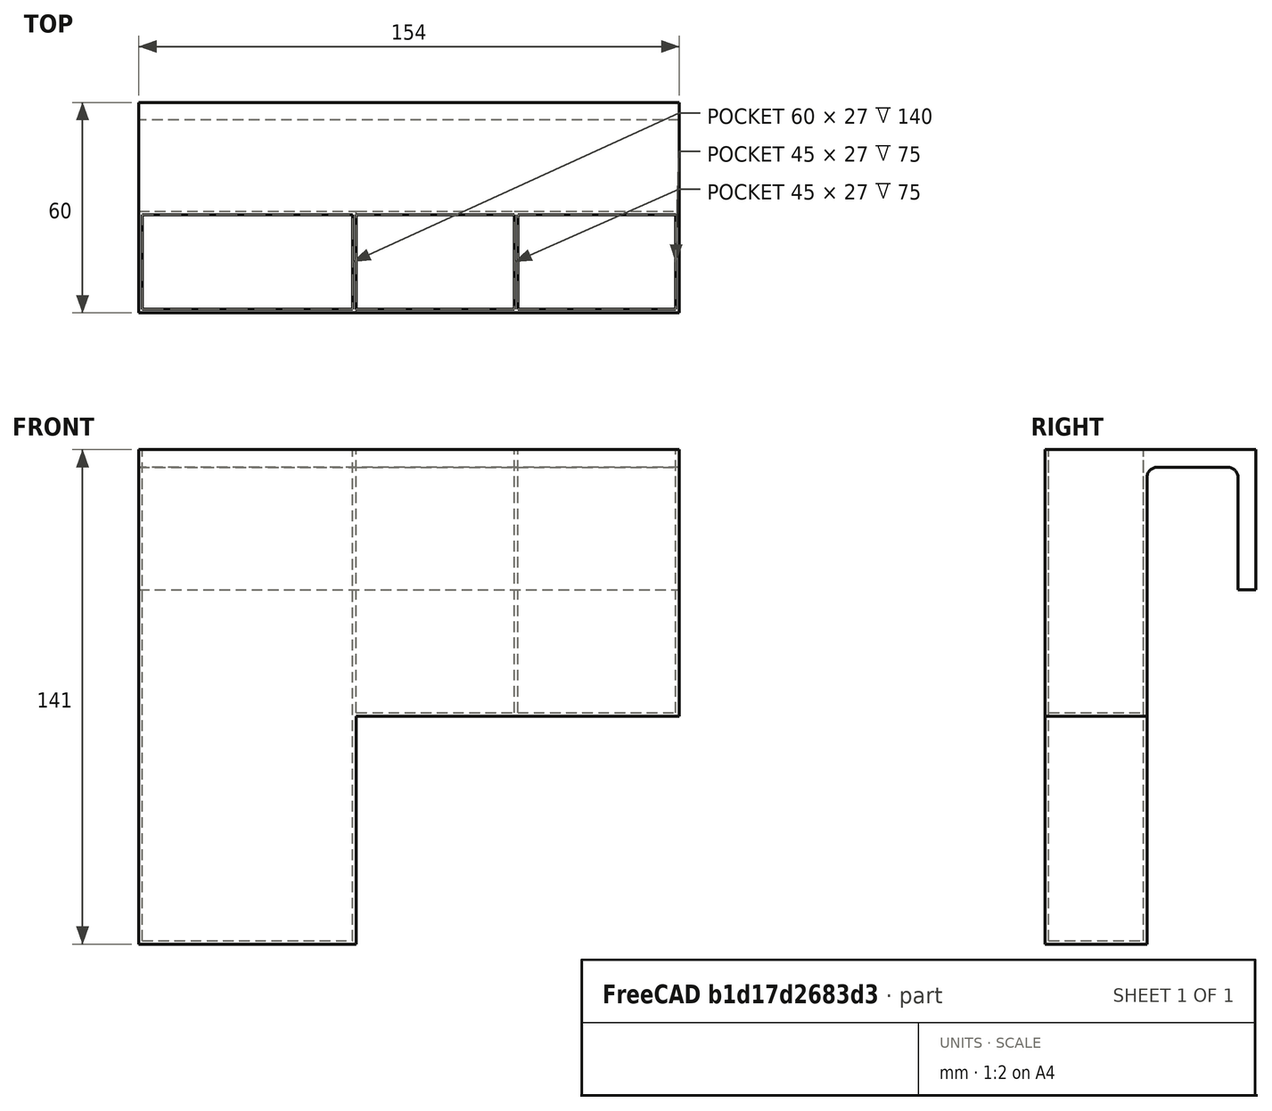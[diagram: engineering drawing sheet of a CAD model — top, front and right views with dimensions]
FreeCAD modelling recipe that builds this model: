
FCSTD DOCUMENT  (FreeCAD 1.0R1.0.1)
Label: TV Remote Holder
License: All rights reserved
LicenseURL: http://en.wikipedia.org/wiki/All_rights_reserved
objects: Part::Box×8, Part::MultiFuse×3, Part::Cut×1, Part::Fillet×1
note: 13 computed .brp shape members not serialized (recipe doc carries the construction recipe); baked Part::Feature solids carry a one-line shape summary decoded from their .brp

FEATURE [Part::Box] Box  label="Cube"
  AttacherType = Attacher::AttachEngine3D
  Height = 141
  Length = 62
  Width = 29
FEATURE [Part::Box] Box001  label="Cube001"
  AttacherType = Attacher::AttachEngine3D
  Height = 140
  Length = 60
  Placement = pos=(1,1,1) rot=(0,0,1;0rad)
  Width = 27
FEATURE [Part::Box] Box002  label="Cube002"
  AttacherType = Attacher::AttachEngine3D
  Height = 76
  Length = 47
  Placement = pos=(61,0,65) rot=(0,0,1;0rad)
  Width = 29
FEATURE [Part::Box] Box003  label="Cube003"
  AttacherType = Attacher::AttachEngine3D
  Height = 75
  Length = 45
  Placement = pos=(62,1,66) rot=(0,0,1;0rad)
  Width = 27
FEATURE [Part::Box] Box004  label="Cube004"
  AttacherType = Attacher::AttachEngine3D
  Height = 76
  Length = 47
  Placement = pos=(107,0,65) rot=(0,0,1;0rad)
  Width = 29
FEATURE [Part::Box] Box005  label="Cube005"
  AttacherType = Attacher::AttachEngine3D
  Height = 75
  Length = 45
  Placement = pos=(108,1,66) rot=(0,0,1;0rad)
  Width = 27
FEATURE [Part::MultiFuse] Fusion
  Shapes = -> [Box,Box002,Box004]
FEATURE [Part::MultiFuse] Fusion001
  Shapes = -> [Box001,Box003,Box005]
FEATURE [Part::Box] Box006  label="Cube006"
  AttacherType = Attacher::AttachEngine3D
  Height = 5
  Length = 154
  Placement = pos=(0,29,136) rot=(0,0,1;0rad)
  Width = 31
FEATURE [Part::Box] Box007  label="Cube007"
  AttacherType = Attacher::AttachEngine3D
  Height = 40
  Length = 154
  Placement = pos=(0,55,101) rot=(0,0,1;0rad)
  Width = 5
FEATURE [Part::MultiFuse] Fusion002
  Shapes = -> [Fusion,Box006,Box007]
FEATURE [Part::Cut] Cut
  Base = -> Fusion002
  Tool = -> Fusion001
FEATURE [Part::Fillet] Fillet
  Base = -> Cut
  EdgeLinks = -> Cut [Edge19,Edge21,Edge23,Edge25]
  Edges = 4 edges r=3: [Edge19,Edge21,Edge23,Edge25]
